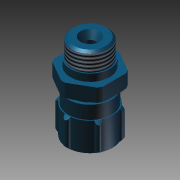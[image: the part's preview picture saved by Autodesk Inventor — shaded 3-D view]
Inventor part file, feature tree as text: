
AUTODESK INVENTOR PART (.ipt)
format: ipt  version: 2011 SP1 (Build 150282100, 282)  size: 255,488 bytes
history: native  units: mm
features: other x7, sketch x7, revolve x5, thread x2, extrude x2
ambient origin geometry x8: Origin, YZ Plane, XZ Plane, XY Plane, X Axis, Y Axis, Z Axis, Center Point
bodies: Solid1 (feature_tree)
feature tree (23):
  revolve  "Revolution1"  Angle=360.0deg
  revolve  "Revolution2"  [1 undecoded]
  thread  "Thread1"  [1 undecoded]
  extrude  "Extrusion1"  Depth=4.319mm TaperAngle=0.0deg
  revolve  "Revolution3"  Angle=360.0deg
  revolve  "Revolution4"  [1 undecoded]
  thread  "Thread2"  [1 undecoded]
  extrude  "Extrusion2"  [1 undecoded]
  revolve  "Revolution5"  [1 undecoded]
  other  "ANBAU_XY"
  other  "ANBAU_YZ"
  other  "ANBAU_ZX"
  other  "ANBAU_X"
  other  "ANBAU_Y"
  other  "ANBAU_Z"
  other  "ANBAU_Center"
  sketch  "Sketch_1"  dims[d0=360.0deg d1=360.0deg]
  sketch  "Sketch_2"  dims[d7=360.0deg d8=4.319mm d9=0.0mm]
  sketch  "Sketch_3"  dims[d10=3.7mm d11=0.0mm d12=360.0deg]
  sketch  "Sketch_4"  dims[d13=0.0mm]
  sketch  "Sketch_5"
  sketch  "Sketch_6"
  sketch  "Sketch_7_ALT_Drilling_1"  dims[d2=5.9585mm d3=0.0mm d4=7.5mm d5=0.0mm d6=360.0deg]
note: 6 required parameter values undecoded (feature->parameter linkage not recoverable at this tier; creation-order binding heuristic only, values carry confidence <= 0.55)